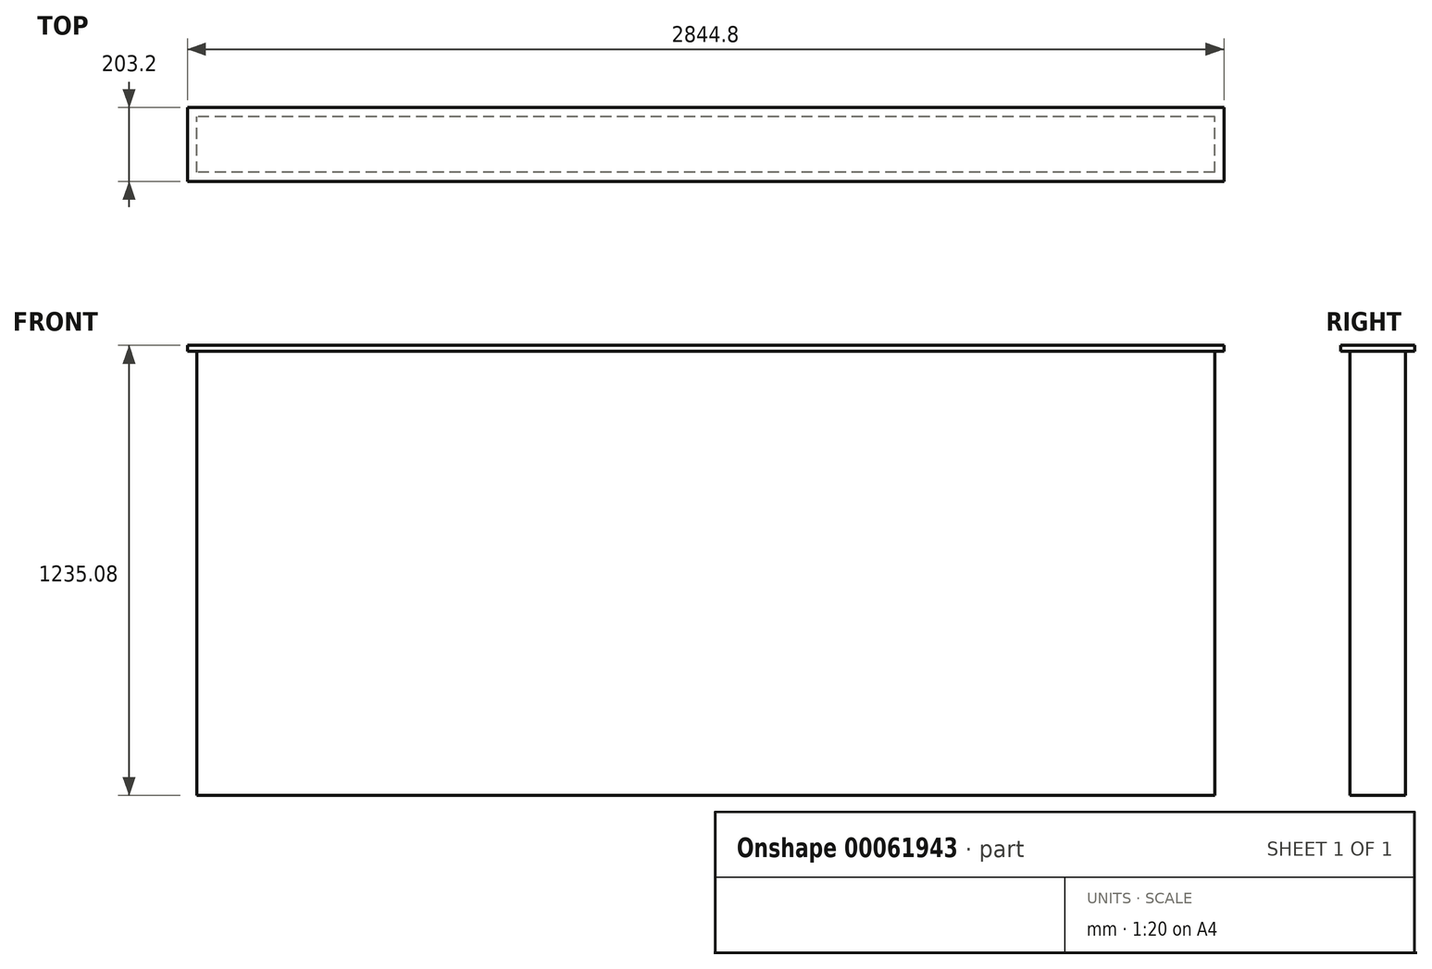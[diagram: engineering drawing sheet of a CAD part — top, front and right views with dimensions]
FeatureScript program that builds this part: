
annotation { "Feature Type Name" : "Feature", "Feature Type Description" : "" }
export const myFeature = defineFeature(function(context is Context, id is Id, definition is map)
    precondition{}
    {
        {
            var Q0;
            Q0=qCreatedBy(makeId("Front.planeOp"),FACE);
            var sketch = newSketch(context, id + "F0", { "sketchPlane" : qUnion([Q0])});
            skLineSegment(sketch, "E0.rect.bottom", {"start": v(1397, -609.6) * mm, "end": v(-1397, -609.6) * mm});
            skLineSegment(sketch, "E0.rect.top", {"start": v(1397, 609.6) * mm, "end": v(-1397, 609.6) * mm});
            skLineSegment(sketch, "E0.rect.left", {"start": v(1397, -609.6) * mm, "end": v(1397, 609.6) * mm});
            skLineSegment(sketch, "E0.rect.right", {"start": v(-1397, -609.6) * mm, "end": v(-1397, 609.6) * mm});
            skPoint(sketch, "E0.rect.middle", {"position": v(0, 0) * mm});
            skSolve(sketch);
        }
        {
            var Q0;
            Q0=makeQuery(id+"F0.imprint","IMPRINT",FACE,{"disambiguationData":[TD([[makeQuery(id+"F0.imprint","IMPRINT",EDGE,{"derivedFrom":sQuery(id+"F0.wireOp",EDGE,"E0.rect.bottom")}),-1.0]])]});
            extrude(context, id + "F1", {"entities" : qUnion([Q0]), "depth" : 152.4 * mm});
        }
        {
            var Q0;
            Q0=makeQuery(id+"F1.opExtrude","SWEPT_FACE",FACE,{"disambiguationData":[OSD([sQuery(id+"F0.wireOp",EDGE,"E0.rect.top")])]});
            var sketch = newSketch(context, id + "F2", { "sketchPlane" : qUnion([Q0])});
            skLineSegment(sketch, "E1.0", {"start": v(1422.4, 25.4) * mm, "end": v(-1422.4, 25.4) * mm});
            skLineSegment(sketch, "E1.1", {"start": v(1422.4, -177.8) * mm, "end": v(1422.4, 25.4) * mm});
            skLineSegment(sketch, "E1.2", {"start": v(-1422.4, -177.8) * mm, "end": v(1422.4, -177.8) * mm});
            skLineSegment(sketch, "E1.3", {"start": v(-1422.4, 25.4) * mm, "end": v(-1422.4, -177.8) * mm});
            skSolve(sketch);
        }
        {
            var Q0;
            {var subQ0=sQuery(id+"F0.wireOp",EDGE,"E0.rect.top");Q0=makeQuery(id+"F2.imprint","IMPRINT",FACE,{"disambiguationData":[TD([[makeQuery(id+"F2.imprint","IMPRINT",EDGE,{"derivedFrom":makeQuery(id+"F1.opExtrude","CAP_EDGE",EDGE,{"disambiguationData":[OSD([subQ0])],"isStart":true})}),1.0]])]});}
            var Q1;
            Q1=makeQuery(id+"F2.imprint","IMPRINT",FACE,{"disambiguationData":[TD([[makeQuery(id+"F2.imprint","IMPRINT",EDGE,{"derivedFrom":sQuery(id+"F2.wireOp",EDGE,"E1.0")}),1.0]])]});
            extrude(context, id + "F3", {"entities" : qUnion([Q0, Q1]), "depth" : 15.88 * mm});
        }
    });
